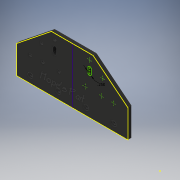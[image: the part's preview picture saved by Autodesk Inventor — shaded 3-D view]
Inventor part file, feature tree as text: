
AUTODESK INVENTOR PART (.ipt)
format: ipt  version: 2017 (Build 210142000, 142)  size: 469,504 bytes
history: native  units: in
note: dims shown in document units (in); Inventor stores cm internally (conversion verified against a paired STEP export)
features: sketch x5, extrude x2, hole x2, projected_geometry x2, pattern_linear x1, plane x1, mirror x1, emboss x1
ambient origin geometry x8: Origin, YZ Plane, XZ Plane, XY Plane, X Axis, Y Axis, Z Axis, Center Point
bodies: Solid1 (feature_tree)
feature tree (15):
  extrude  "Extrusion1"  Depth=2.0in
  hole  "Hole1"  [1 undecoded]
  pattern_linear  "Rectangular Pattern1"  Spacing1=0.5in  [1 undecoded]
  sketch  "Sketch3"  dims[d4=3.0in]
  hole  "Hole2"  [1 undecoded]
  extrude  "Extrusion2"  Depth=0.1in
  sketch  "Sketch4"  dims[d5=2.5in]
  plane  "Work Plane1"
  mirror  "Mirror1"
  emboss  "Emboss1"
  sketch  "Sketch1"  dims[d0=8.0in d1=2.0in]
  sketch  "Sketch2"  dims[d2=2.0in d3=4.0in]
  projected_geometry  "Projected Loop1"
  projected_geometry  "Projected Loop2"
  sketch  "Sketch5"  dims[d6=0.25in d7=0.0in d8=0.5in d9=1.0in d10=0.196in d11=0.5in d12=0.375in d13=0.05in d14=0.5635in d15=0.75in d16=0.8108in d17=1.5748in d19=2.0in d20=0.25in d21=0.196in d22=0.5in d23=0.375in d24=0.25in d25=0.5635in d26=0.75in d27=0.8108in d28=1.0in d29=0.0in d30=0.0in d31=0.1in d32=0.0in]
note: 3 required parameter values undecoded (feature->parameter linkage not recoverable at this tier; creation-order binding heuristic only, values carry confidence <= 0.55)
